# Revit family: ledporch-e2-re120-3_5w-830_840_531000019500_491e
name_source: partatom
category: Lighting Fixtures
units: mm (PartAtom-declared; Revit-internal decimal feet)

## family parameters
Cut with Voids When Loaded = No
Host = Face
Light Source = No
Part Type = Normal
Room Calculation Point = No
Round Connector Dimension = Use Diameter
Shared = No

## types (1)
- LEDPorch-E2-Re120-3/5W-830/840 (1 x LED, 600 lm, 4000)
    Apparent Load = 3 VA
    Approval mark = CE
    CIE Flux Codes = 42 72 90 94 100
    Color Rendering = 80
    Color Temperature = 4000
    Control Gear = Electronic ballast
    Default Elevation = 1800 mm
    Description = Porchlight EcoMax G2 3/5W-360/600lm-3/4000K-IP65
    Frequency = 60 Hz
    Height = 82 mm  [stored 0.269029 ft]
    Lamp = 1 x LED
    Lamp Light Flux = 600 lm
    Lamp count = 1
    Length = 345 mm
    Luminous efficacy = 200 lm/W
    Manufacturer = OPPLE
    ModVariant = No
    Model = 531000019500
    Number of Poles = 1
    OnlyDefault = Yes
    Power Factor = 1
    Product Name = LEDPorch-E2-Re120-3/5W-830/840
    Product group = Ceiling / wall-mounted luminaires
    ProductGroupID = 30
    Protection Class = Protection class II
    Protection Degree = IP 65
    RLX_Detail_Level = 1
    RLX_Emergency_Light_Flux = 0 lm
    RLX_Emergency_Type = 0
    RLX_Emergency_Type_DB = No
    RlxData = <blob elided: 244969 chars, md5=5b4e13dc>
    Socket = socket
    Standby Power = 0 W
    System Light Flux = 600 lm
    System Power = 3 W
    Type Comments = Product without accessories
    Type Image = web_porch_e2.jpg
    URL = http://relux.com
    VarID = ---
    Voltage = 230 V
    Voltage Range = 220-240 V
    Weight = 0.00 kg
    Width = 123 mm

note: [stored X ft] marks values corroborated as IEEE doubles in the binary element streams (Revit-internal decimal feet)

## geometry (parser evidence)
native form markers: Sweep x11
no freeform markers — native parametric forms only
